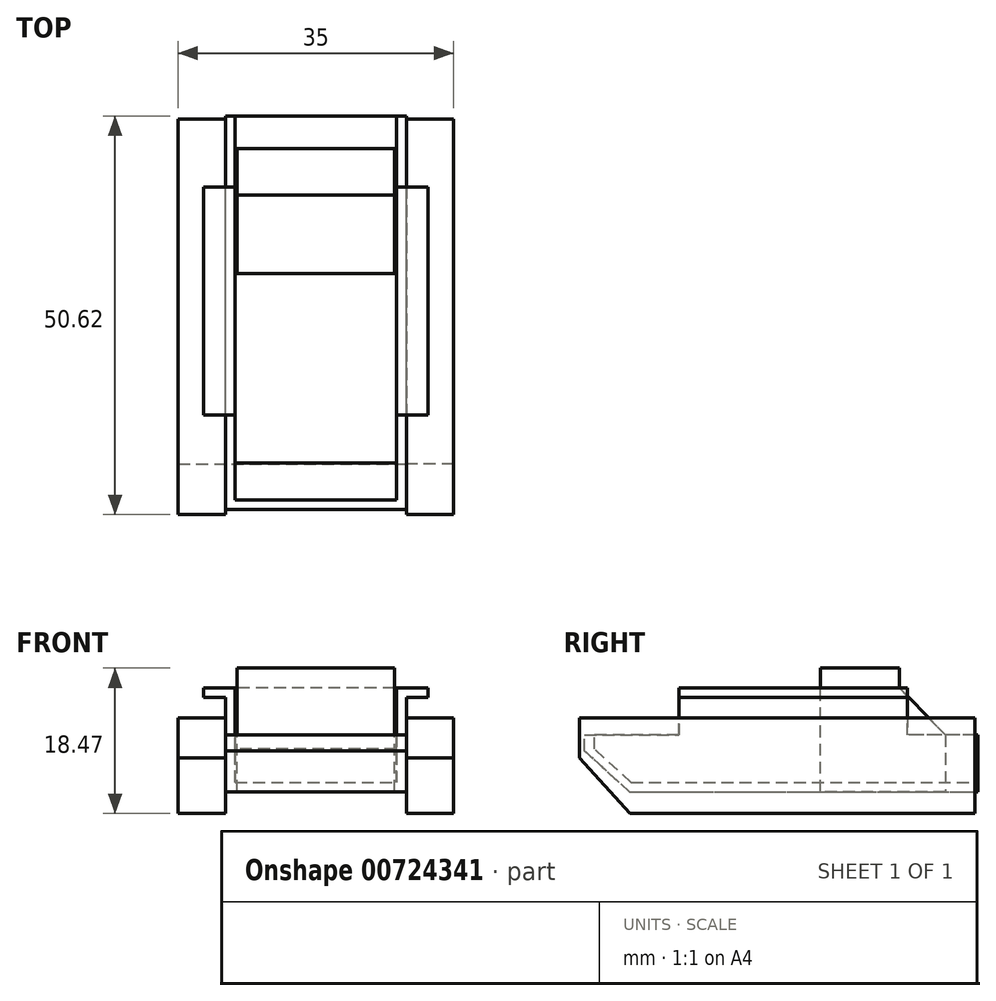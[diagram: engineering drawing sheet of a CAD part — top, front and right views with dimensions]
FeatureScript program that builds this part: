
annotation { "Feature Type Name" : "Feature", "Feature Type Description" : "" }
export const myFeature = defineFeature(function(context is Context, id is Id, definition is map)
    precondition{}
    {
        {
            var Q0;
            Q0=qCreatedBy(makeId("Front.planeOp"),FACE);
            var sketch = newSketch(context, id + "F0", { "sketchPlane" : qUnion([Q0])});
            skLineSegment(sketch, "E0.top", {"start": v(10.25, -6) * mm, "end": v(-10.25, -6) * mm});
            skLineSegment(sketch, "E0.left", {"start": v(10.25, 6) * mm, "end": v(10.25, -6) * mm});
            skLineSegment(sketch, "E0.right", {"start": v(-10.25, 6) * mm, "end": v(-10.25, -6) * mm});
            skPoint(sketch, "E0.middle", {"position": v(0, 0) * mm});
            skLineSegment(sketch, "E1", {"start": v(10.25, 6) * mm, "end": v(14.25, 6) * mm});
            skLineSegment(sketch, "E2", {"start": v(14.25, 6) * mm, "end": v(14.25, 4.75) * mm});
            skLineSegment(sketch, "E3", {"start": v(14.25, 4.75) * mm, "end": v(11.5, 4.75) * mm});
            skLineSegment(sketch, "E4", {"start": v(11.5, 4.75) * mm, "end": v(11.5, -7.25) * mm});
            skLineSegment(sketch, "E5", {"start": v(11.5, -7.25) * mm, "end": v(-11.5, -7.25) * mm});
            skLineSegment(sketch, "E6", {"start": v(-11.5, -7.25) * mm, "end": v(-11.5, 4.75) * mm});
            skLineSegment(sketch, "E7", {"start": v(-11.5, 4.75) * mm, "end": v(-14.25, 4.75) * mm});
            skLineSegment(sketch, "E8", {"start": v(-14.25, 4.75) * mm, "end": v(-14.25, 6) * mm});
            skLineSegment(sketch, "E9", {"start": v(-14.25, 6) * mm, "end": v(-10.25, 6) * mm});
            skSolve(sketch);
        }
        {
            var Q0;
            Q0=makeQuery(id+"F0.imprint","IMPRINT",FACE,{"disambiguationData":[TD([[makeQuery(id+"F0.imprint","IMPRINT",EDGE,{"derivedFrom":sQuery(id+"F0.wireOp",EDGE,"E0.top")}),1.0]])]});
            extrude(context, id + "F1", {"entities" : qUnion([Q0]), "depth" : 50 * mm, "offsetDistance" : 25 * mm});
        }
        {
            var Q0;
            Q0=qCreatedBy(makeId("Right.planeOp"),FACE);
            var sketch = newSketch(context, id + "F2", { "sketchPlane" : qUnion([Q0])});
            skLineSegment(sketch, "E10", {"start": v(0, 0) * mm, "end": v(-9, 0) * mm});
            skLineSegment(sketch, "E11", {"start": v(-9, 0) * mm, "end": v(-9, 8.9) * mm});
            skLineSegment(sketch, "E12", {"start": v(-9, 8.9) * mm, "end": v(-38, 8.9) * mm});
            skLineSegment(sketch, "E13", {"start": v(-38, 8.9) * mm, "end": v(-38, 0) * mm});
            skLineSegment(sketch, "E14", {"start": v(-38, 0) * mm, "end": v(-50, 0) * mm});
            skLineSegment(sketch, "E15", {"start": v(-50, 0) * mm, "end": v(-50, -2) * mm});
            skLineSegment(sketch, "E16", {"start": v(-50, -2) * mm, "end": v(-43.47, -8) * mm});
            skLineSegment(sketch, "E17", {"start": v(-43.47, -8) * mm, "end": v(-52.4, -8) * mm});
            skLineSegment(sketch, "E18", {"start": v(-52.4, -8) * mm, "end": v(-52.4, 11.73) * mm});
            skLineSegment(sketch, "E19", {"start": v(-52.4, 11.73) * mm, "end": v(2.34, 11.73) * mm});
            skLineSegment(sketch, "E20", {"start": v(2.34, 11.73) * mm, "end": v(2.34, 0) * mm});
            skLineSegment(sketch, "E21", {"start": v(2.34, 0) * mm, "end": v(0, 0) * mm});
            skSolve(sketch);
        }
        {
            var Q0;
            Q0=makeQuery(id+"F2.imprint","IMPRINT",FACE,{"disambiguationData":[TD([[makeQuery(id+"F2.imprint","IMPRINT",EDGE,{"derivedFrom":sQuery(id+"F2.wireOp",EDGE,"E10")}),-1.0]])]});
            extrude(context, id + "F3", {"entities" : qUnion([Q0]), "operationType" : NewBodyOperationType.REMOVE, "endBound" : BoundingType.SYMMETRIC, "oppositeDirection" : true, "depth" : 50 * mm, "offsetDistance" : 25 * mm});
        }
        {
            var Q0;
            Q0=qCreatedBy(makeId("Right.planeOp"),FACE);
            var sketch = newSketch(context, id + "F4", { "sketchPlane" : qUnion([Q0])});
            skLineSegment(sketch, "E22", {"start": v(-50, 0) * mm, "end": v(-48.75, 0) * mm});
            skLineSegment(sketch, "E23", {"start": v(-48.75, 0) * mm, "end": v(-48.75, -1.77) * mm});
            skLineSegment(sketch, "E24", {"start": v(-48.75, -1.77) * mm, "end": v(-42.7, -7.25) * mm});
            skLineSegment(sketch, "E25", {"start": v(-42.7, -7.25) * mm, "end": v(-44.28, -7.25) * mm});
            skLineSegment(sketch, "E26", {"start": v(-44.28, -7.25) * mm, "end": v(-50, -2) * mm});
            skLineSegment(sketch, "E27", {"start": v(-50, -2) * mm, "end": v(-50, 0) * mm});
            skSolve(sketch);
        }
        {
            var Q0;
            Q0=makeQuery(id+"F4.imprint","IMPRINT",FACE,{"disambiguationData":[TD([[makeQuery(id+"F4.imprint","IMPRINT",EDGE,{"derivedFrom":sQuery(id+"F4.wireOp",EDGE,"E22")}),-1.0]])]});
            extrude(context, id + "F5", {"entities" : qUnion([Q0]), "operationType" : NewBodyOperationType.ADD, "endBound" : BoundingType.SYMMETRIC, "depth" : 23 * mm, "offsetDistance" : 25 * mm});
        }
        {
            var Q0;
            Q0=qCreatedBy(makeId("Right.planeOp"),FACE);
            var sketch = newSketch(context, id + "F6", { "sketchPlane" : qUnion([Q0])});
            skLineSegment(sketch, "E28", {"start": v(-20.01, 6) * mm, "end": v(-20.01, 8.5) * mm});
            skLineSegment(sketch, "E29", {"start": v(-20.01, 8.5) * mm, "end": v(-10.01, 8.5) * mm});
            skLineSegment(sketch, "E30", {"start": v(-10.01, 8.5) * mm, "end": v(-10.01, 5.99) * mm});
            skLineSegment(sketch, "E31", {"start": v(-10.01, 5.99) * mm, "end": v(-4.15, 0) * mm});
            skLineSegment(sketch, "E32", {"start": v(-4.15, 0) * mm, "end": v(-4.15, -7.2) * mm});
            skLineSegment(sketch, "E33", {"start": v(-4.15, -7.2) * mm, "end": v(-20.01, -7.2) * mm});
            skLineSegment(sketch, "E34", {"start": v(-20.01, -7.2) * mm, "end": v(-20.01, 6) * mm});
            skLineSegment(sketch, "E35", {"start": v(-20.01, -7.2) * mm, "end": v(-20.01, -7.2) * mm});
            skSolve(sketch);
        }
        {
            var Q0;
            Q0=makeQuery(id+"F6.imprint","IMPRINT",FACE,{"disambiguationData":[TD([[makeQuery(id+"F6.imprint","IMPRINT",EDGE,{"derivedFrom":sQuery(id+"F6.wireOp",EDGE,"E28")}),-1.0]])]});
            var Q1;
            Q1=sQuery(id+"F6.wireOp",EDGE,"E33");
            var Q2;
            Q2=sQuery(id+"F6.wireOp",EDGE,"E32");
            var Q3;
            Q3=sQuery(id+"F6.wireOp",EDGE,"E29");
            var Q4;
            Q4=sQuery(id+"F6.wireOp",EDGE,"E28");
            var Q5;
            Q5=sQuery(id+"F6.wireOp",EDGE,"E31");
            var Q6;
            Q6=sQuery(id+"F6.wireOp",EDGE,"E34");
            var Q7;
            Q7=sQuery(id+"F6.wireOp",EDGE,"E30");
            extrude(context, id + "F7", {"entities" : qUnion([Q0]), "surfaceEntities" : qUnion([Q1, Q2, Q3, Q4, Q5, Q6, Q7]), "endBound" : BoundingType.SYMMETRIC, "depth" : 20 * mm, "offsetDistance" : 25 * mm});
        }
        {
            var Q0;
            Q0=makeQuery(id+"F1.opExtrude","SWEPT_FACE",FACE,{"disambiguationData":[OSD([sQuery(id+"F0.wireOp",EDGE,"E4")])]});
            var sketch = newSketch(context, id + "F8", { "sketchPlane" : qUnion([Q0])});
            skLineSegment(sketch, "E36", {"start": v(-38, 4.67) * mm, "end": v(-38, 2.17) * mm});
            skLineSegment(sketch, "E37", {"start": v(-38, 2.17) * mm, "end": v(-50.62, 2.17) * mm});
            skLineSegment(sketch, "E38", {"start": v(-50.62, 2.17) * mm, "end": v(-50.62, -2.92) * mm});
            skLineSegment(sketch, "E39", {"start": v(-50.62, -2.92) * mm, "end": v(-44.2, -9.96) * mm});
            skLineSegment(sketch, "E40", {"start": v(-44.2, -9.96) * mm, "end": v(-0.41, -9.96) * mm});
            skLineSegment(sketch, "E41", {"start": v(-0.41, -9.96) * mm, "end": v(-0.41, 2.17) * mm});
            skLineSegment(sketch, "E42", {"start": v(-0.41, 2.17) * mm, "end": v(-38, 2.17) * mm});
            skSolve(sketch);
        }
        {
            var Q0;
            Q0=qSketchRegion(id+"F8",true);
            extrude(context, id + "F9", {"entities" : qUnion([Q0]), "operationType" : NewBodyOperationType.ADD, "depth" : 6 * mm, "offsetDistance" : 25 * mm});
        }
        {
            var Q0;
            Q0=makeQuery(id+"F1.opExtrude","SWEPT_BODY",BODY,{"disambiguationData":[OSD([sQuery(id+"F0.wireOp",EDGE,"E0.top"),sQuery(id+"F0.wireOp",EDGE,"E0.left"),sQuery(id+"F0.wireOp",EDGE,"E0.right"),sQuery(id+"F0.wireOp",EDGE,"E1"),sQuery(id+"F0.wireOp",EDGE,"E2"),sQuery(id+"F0.wireOp",EDGE,"E3"),sQuery(id+"F0.wireOp",EDGE,"E4"),sQuery(id+"F0.wireOp",EDGE,"E5"),sQuery(id+"F0.wireOp",EDGE,"E6"),sQuery(id+"F0.wireOp",EDGE,"E7"),sQuery(id+"F0.wireOp",EDGE,"E8"),sQuery(id+"F0.wireOp",EDGE,"E9")])]});
            var Q1;
            Q1=qCreatedBy(makeId("Right.planeOp"),FACE);
            mirror(context, id + "F10", {"entities" : qUnion([Q0]), "mirrorPlane" : qUnion([Q1])});
        }
    });
